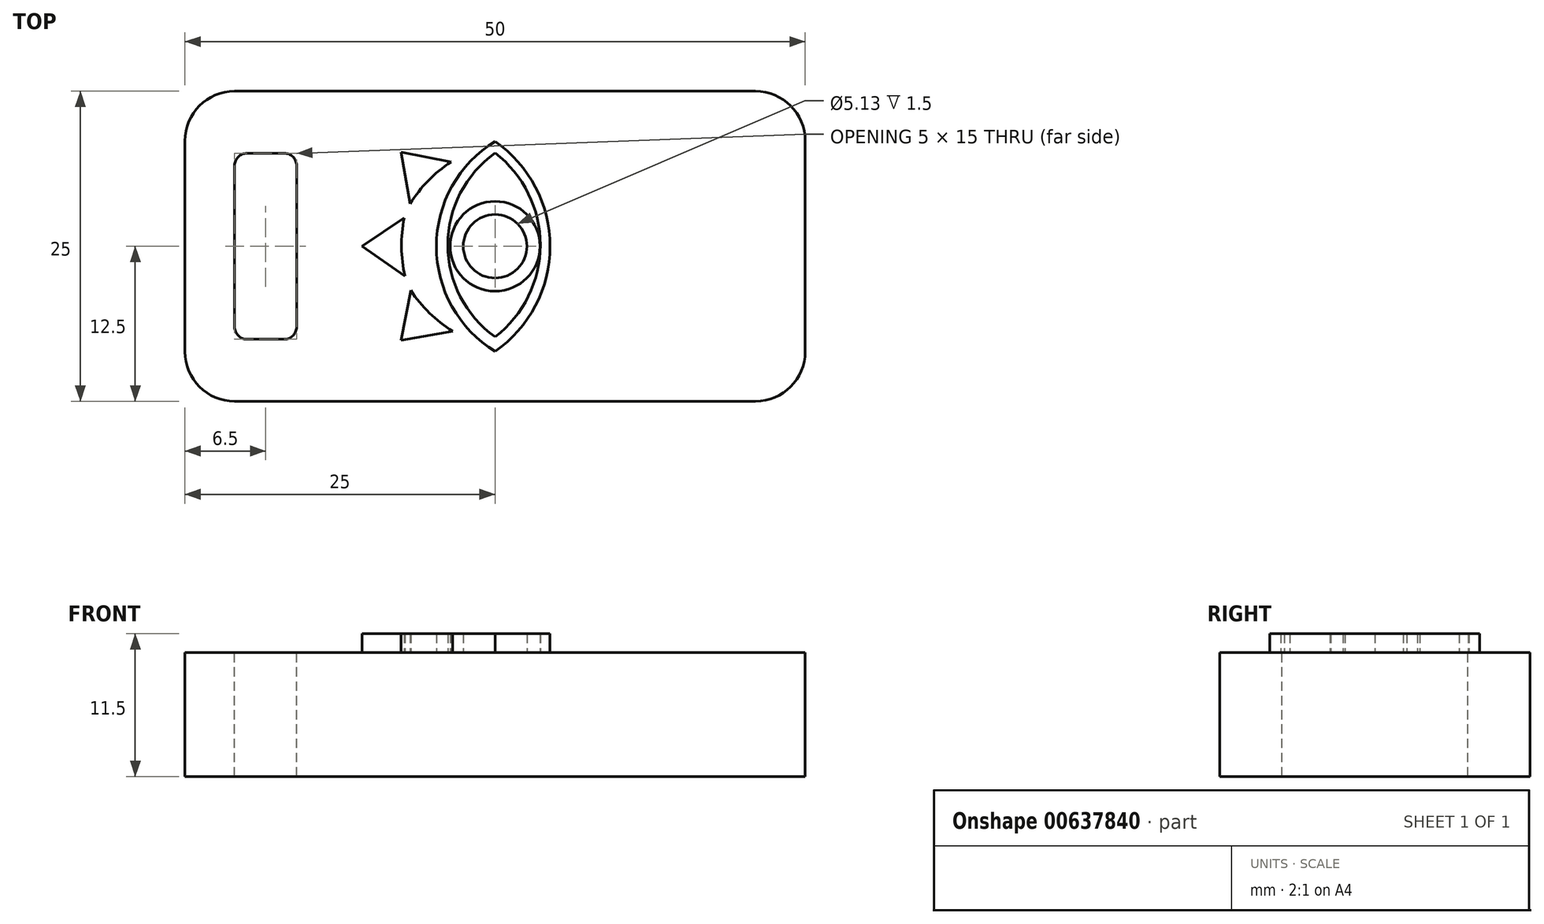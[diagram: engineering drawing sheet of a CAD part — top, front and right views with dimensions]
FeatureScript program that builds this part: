
annotation { "Feature Type Name" : "Feature", "Feature Type Description" : "" }
export const myFeature = defineFeature(function(context is Context, id is Id, definition is map)
    precondition{}
    {
        {
            var Q0;
            Q0=qCreatedBy(makeId("Top.planeOp"),FACE);
            var sketch = newSketch(context, id + "F0", { "sketchPlane" : qUnion([Q0])});
            skLineSegment(sketch, "E0.bottom", {"start": v(-25, 12.5) * mm, "end": v(25, 12.5) * mm});
            skLineSegment(sketch, "E0.top", {"start": v(-25, -12.5) * mm, "end": v(25, -12.5) * mm});
            skLineSegment(sketch, "E0.left", {"start": v(-25, 12.5) * mm, "end": v(-25, -12.5) * mm});
            skLineSegment(sketch, "E0.right", {"start": v(25, 12.5) * mm, "end": v(25, -12.5) * mm});
            skSolve(sketch);
        }
        {
            var Q0;
            Q0=makeQuery(id+"F0.imprint","IMPRINT",FACE,{"disambiguationData":[TD([[makeQuery(id+"F0.imprint","IMPRINT",EDGE,{"derivedFrom":sQuery(id+"F0.wireOp",EDGE,"E0.bottom")}),-1.0]])]});
            extrude(context, id + "F1", {"entities" : qUnion([Q0]), "depth" : 10 * mm, "offsetDistance" : 25 * mm});
        }
        {
            var Q0;
            Q0=makeQuery(id+"F1.opExtrude","SWEPT_EDGE",EDGE,{"disambiguationData":[OSD([sQuery(id+"F0.wireOp",EDGE,"E0.top"),sQuery(id+"F0.wireOp",EDGE,"E0.left")])]});
            var Q1;
            Q1=makeQuery(id+"F1.opExtrude","SWEPT_EDGE",EDGE,{"disambiguationData":[OSD([sQuery(id+"F0.wireOp",EDGE,"E0.top"),sQuery(id+"F0.wireOp",EDGE,"E0.right")])]});
            var Q2;
            Q2=makeQuery(id+"F1.opExtrude","SWEPT_EDGE",EDGE,{"disambiguationData":[OSD([sQuery(id+"F0.wireOp",EDGE,"E0.bottom"),sQuery(id+"F0.wireOp",EDGE,"E0.right")])]});
            var Q3;
            Q3=makeQuery(id+"F1.opExtrude","SWEPT_EDGE",EDGE,{"disambiguationData":[OSD([sQuery(id+"F0.wireOp",EDGE,"E0.bottom"),sQuery(id+"F0.wireOp",EDGE,"E0.left")])]});
            fillet(context, id + "F2", {"entities" : qUnion([Q0, Q1, Q2, Q3]), "radius" : 4 * mm, "tangentPropagation" : true, "allowEdgeOverflow" : false});
        }
        {
            var Q0;
            Q0=makeQuery(id+"F1.opExtrude","CAP_FACE",FACE,{"disambiguationData":[OSD([sQuery(id+"F0.wireOp",EDGE,"E0.bottom"),sQuery(id+"F0.wireOp",EDGE,"E0.top"),sQuery(id+"F0.wireOp",EDGE,"E0.left"),sQuery(id+"F0.wireOp",EDGE,"E0.right")])],"isStart":false});
            var sketch = newSketch(context, id + "F3", { "sketchPlane" : qUnion([Q0])});
            skLineSegment(sketch, "E1.bottom", {"start": v(-21, 7.5) * mm, "end": v(-16, 7.5) * mm});
            skLineSegment(sketch, "E1.top", {"start": v(-21, -7.5) * mm, "end": v(-16, -7.5) * mm});
            skLineSegment(sketch, "E1.left", {"start": v(-21, 7.5) * mm, "end": v(-21, -7.5) * mm});
            skLineSegment(sketch, "E1.right", {"start": v(-16, 7.5) * mm, "end": v(-16, -7.5) * mm});
            skSolve(sketch);
        }
        {
            var Q0;
            Q0 = qSketchRegion(id + "F3", true);
            extrude(context, id + "F4", {"entities" : qUnion([Q0]), "operationType" : NewBodyOperationType.REMOVE, "oppositeDirection" : true, "depth" : 25 * mm, "offsetDistance" : 25 * mm});
        }
        {
            var Q0;
            Q0=makeQuery(id+"F4.boolean.opBoolean","COPY",EDGE,{"derivedFrom":makeQuery(id+"F4.opExtrude","SWEPT_EDGE",EDGE,{"disambiguationData":[OSD([sQuery(id+"F3.wireOp",EDGE,"E1.bottom"),sQuery(id+"F3.wireOp",EDGE,"E1.left")])]})});
            var Q1;
            Q1=makeQuery(id+"F4.boolean.opBoolean","COPY",EDGE,{"derivedFrom":makeQuery(id+"F4.opExtrude","SWEPT_EDGE",EDGE,{"disambiguationData":[OSD([sQuery(id+"F3.wireOp",EDGE,"E1.top"),sQuery(id+"F3.wireOp",EDGE,"E1.left")])]})});
            var Q2;
            Q2=makeQuery(id+"F4.boolean.opBoolean","COPY",EDGE,{"derivedFrom":makeQuery(id+"F4.opExtrude","SWEPT_EDGE",EDGE,{"disambiguationData":[OSD([sQuery(id+"F3.wireOp",EDGE,"E1.bottom"),sQuery(id+"F3.wireOp",EDGE,"E1.right")])]})});
            var Q3;
            Q3=makeQuery(id+"F4.boolean.opBoolean","COPY",EDGE,{"derivedFrom":makeQuery(id+"F4.opExtrude","SWEPT_EDGE",EDGE,{"disambiguationData":[OSD([sQuery(id+"F3.wireOp",EDGE,"E1.top"),sQuery(id+"F3.wireOp",EDGE,"E1.right")])]})});
            fillet(context, id + "F5", {"entities" : qUnion([Q0, Q1, Q2, Q3]), "radius" : 1 * mm, "tangentPropagation" : true, "allowEdgeOverflow" : false});
        }
        {
            var Q0;
            Q0=makeQuery(id+"F1.opExtrude","CAP_FACE",FACE,{"disambiguationData":[OSD([sQuery(id+"F0.wireOp",EDGE,"E0.bottom"),sQuery(id+"F0.wireOp",EDGE,"E0.top"),sQuery(id+"F0.wireOp",EDGE,"E0.left"),sQuery(id+"F0.wireOp",EDGE,"E0.right")])],"isStart":false});
            var sketch = newSketch(context, id + "F6", { "sketchPlane" : qUnion([Q0])});
            skArc(sketch, "E2", {"start": v(0, 7.52) * mm, "mid": v(-3.81, 0.1) * mm, "end": v(0, -7.31) * mm});
            skArc(sketch, "E3", {"start": v(0, -7.31) * mm, "mid": v(3.65, 0.1) * mm, "end": v(0, 7.52) * mm});
            skCircle(sketch, "E4", {"center": v(0, 0) * mm, "radius": 3.62 * mm});
            skCircle(sketch, "E5", {"center": v(0, 0) * mm, "radius": 2.56 * mm});
            skArc(sketch, "E6", {"start": v(0, 8.46) * mm, "mid": v(-4.73, 0) * mm, "end": v(0, -8.48) * mm});
            skArc(sketch, "E7", {"start": v(0, -8.48) * mm, "mid": v(4.43, 0) * mm, "end": v(0, 8.46) * mm});
            skArc(sketch, "E8", {"start": v(-7.33, 2.28) * mm, "mid": v(-7.55, -0.07) * mm, "end": v(-7.26, -2.42) * mm});
            skLineSegment(sketch, "E9", {"start": v(-7.26, -2.42) * mm, "end": v(-10.73, 0) * mm});
            skLineSegment(sketch, "E10", {"start": v(-10.73, 0) * mm, "end": v(-7.33, 2.28) * mm});
            skLineSegment(sketch, "E11.1.0", {"start": v(-3.42, -6.85) * mm, "end": v(-7.59, -7.59) * mm});
            skArc(sketch, "E11.1.1", {"start": v(-6.8, -3.56) * mm, "mid": v(-5.29, -5.39) * mm, "end": v(-3.42, -6.85) * mm});
            skLineSegment(sketch, "E11.1.2", {"start": v(-7.59, -7.59) * mm, "end": v(-6.8, -3.56) * mm});
            skLineSegment(sketch, "E11.anchor1", {"start": v(0, 0) * mm, "end": v(-10.73, 0) * mm, "construction": true});
            skLineSegment(sketch, "E11.anchor2", {"start": v(0, 0) * mm, "end": v(-7.59, -7.59) * mm, "construction": true});
            skLineSegment(sketch, "E12.1.0", {"start": v(-7.59, 7.59) * mm, "end": v(-3.56, 6.8) * mm});
            skLineSegment(sketch, "E12.1.1", {"start": v(-6.85, 3.42) * mm, "end": v(-7.59, 7.59) * mm});
            skArc(sketch, "E12.1.2", {"start": v(-3.56, 6.8) * mm, "mid": v(-5.39, 5.29) * mm, "end": v(-6.85, 3.42) * mm});
            skLineSegment(sketch, "E12.anchor2", {"start": v(0, 0) * mm, "end": v(-7.59, 7.59) * mm, "construction": true});
            skSolve(sketch);
        }
        {
            var Q0;
            Q0=makeQuery(id+"F6.imprint","IMPRINT",FACE,{"disambiguationData":[TD([[makeQuery(id+"F6.imprint","IMPRINT",EDGE,{"derivedFrom":sQuery(id+"F6.wireOp",EDGE,"E4")}),1.0]])]});
            var Q1;
            Q1=makeQuery(id+"F6.imprint","IMPRINT",FACE,{"disambiguationData":[TD([[makeQuery(id+"F6.imprint","IMPRINT",EDGE,{"derivedFrom":sQuery(id+"F6.wireOp",EDGE,"E2")}),-1.0]])]});
            var Q2;
            Q2=makeQuery(id+"F6.imprint","IMPRINT",FACE,{"disambiguationData":[TD([[makeQuery(id+"F6.imprint","IMPRINT",EDGE,{"derivedFrom":sQuery(id+"F6.wireOp",EDGE,"E11.1.0")}),-1.0]])]});
            var Q3;
            Q3=makeQuery(id+"F6.imprint","IMPRINT",FACE,{"disambiguationData":[TD([[makeQuery(id+"F6.imprint","IMPRINT",EDGE,{"derivedFrom":sQuery(id+"F6.wireOp",EDGE,"E8")}),-1.0]])]});
            var Q4;
            Q4=makeQuery(id+"F6.imprint","IMPRINT",FACE,{"disambiguationData":[TD([[makeQuery(id+"F6.imprint","IMPRINT",EDGE,{"derivedFrom":sQuery(id+"F6.wireOp",EDGE,"E12.1.0")}),-1.0]])]});
            extrude(context, id + "F7", {"entities" : qUnion([Q0, Q1, Q2, Q3, Q4]), "operationType" : NewBodyOperationType.ADD, "depth" : 1.5 * mm, "offsetDistance" : 25 * mm});
        }
    });
